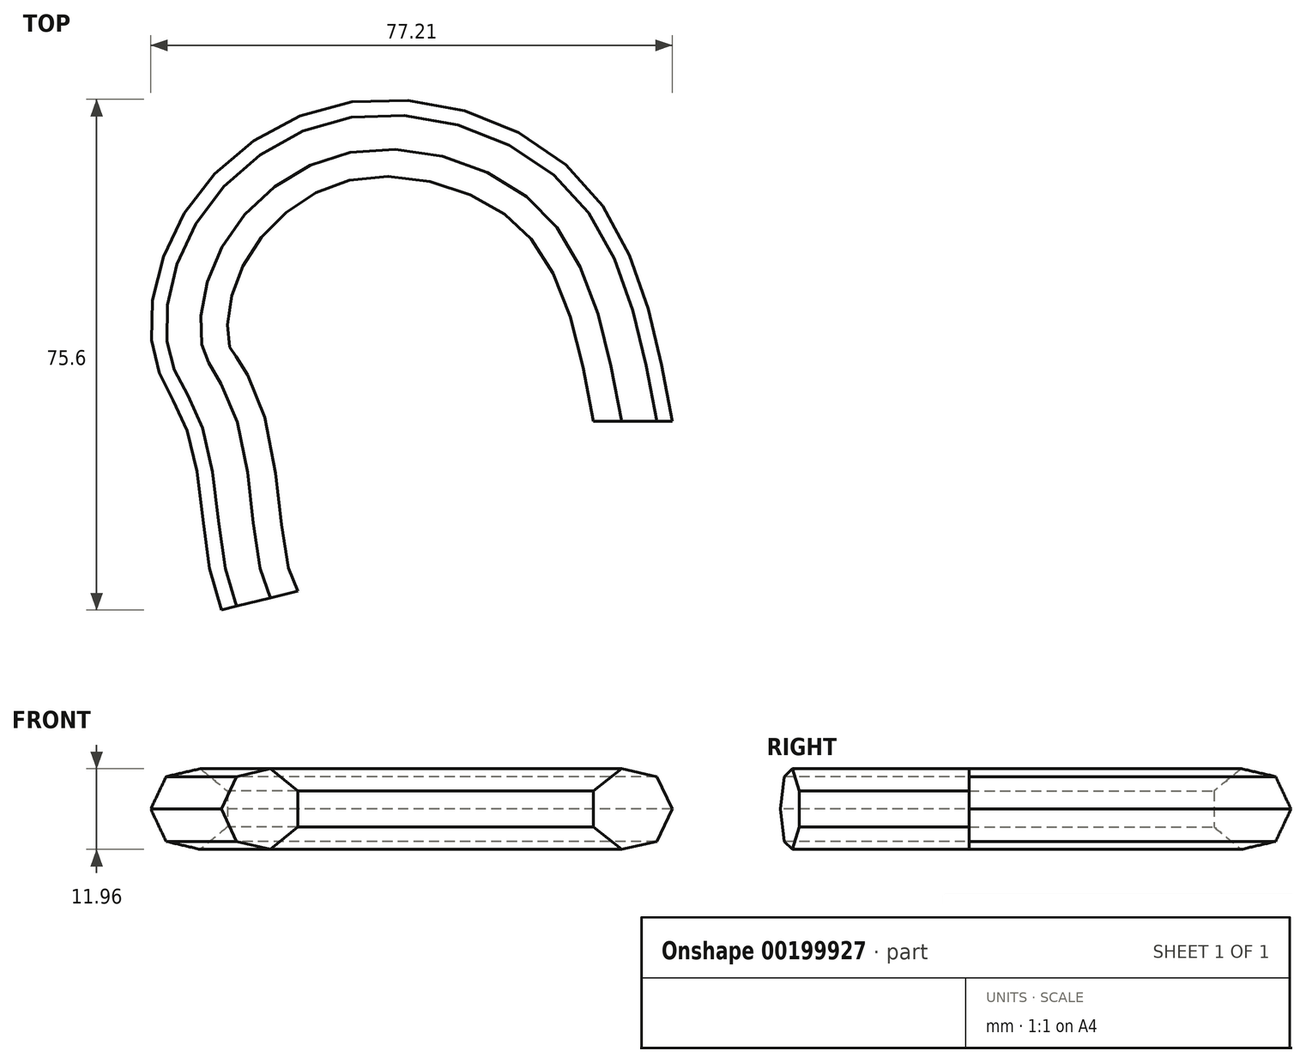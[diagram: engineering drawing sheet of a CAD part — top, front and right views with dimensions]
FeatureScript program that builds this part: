
annotation { "Feature Type Name" : "Feature", "Feature Type Description" : "" }
export const myFeature = defineFeature(function(context is Context, id is Id, definition is map)
    precondition{}
    {
        {
            var Q0;
            Q0=qCreatedBy(makeId("Top.planeOp"),FACE);
            var sketch = newSketch(context, id + "F0", { "sketchPlane" : qUnion([Q0])});
            skFitSpline(sketch, "E0", {"points": [v(56.92, 0) * mm, v(43.69, 35.53) * mm, v(8.92, 47.23) * mm, v(-16, 29.69) * mm, v(-19.7, 9.08) * mm, v(-14.46, -2.62) * mm, v(-9.83, -27.93) * mm], "startDerivative": vector(-33.46, 187.5) * mm, "endDerivative": vector(53.48, -120.24) * mm});
            skLineSegment(sketch, "E1", {"start": v(0, 0) * mm, "end": v(56.92, 0) * mm, "construction": true});
            skSolve(sketch);
        }
        {
            var Q0;
            Q0=qCreatedBy(makeId("Front.planeOp"),FACE);
            var sketch = newSketch(context, id + "F1", { "sketchPlane" : qUnion([Q0])});
            skCircle(sketch, "E2.cCircle", {"center": v(50.79, 0) * mm, "radius": 5.52 * mm, "construction": true});
            skLineSegment(sketch, "E2.0", {"start": v(56.92, 0) * mm, "end": v(54.6, -4.8) * mm});
            skLineSegment(sketch, "E2.1", {"start": v(54.6, -4.8) * mm, "end": v(49.42, -5.98) * mm});
            skLineSegment(sketch, "E2.2", {"start": v(49.42, -5.98) * mm, "end": v(45.26, -2.66) * mm});
            skLineSegment(sketch, "E2.3", {"start": v(45.26, -2.66) * mm, "end": v(45.26, 2.66) * mm});
            skLineSegment(sketch, "E2.4", {"start": v(45.26, 2.66) * mm, "end": v(49.42, 5.98) * mm});
            skLineSegment(sketch, "E2.5", {"start": v(49.42, 5.98) * mm, "end": v(54.6, 4.8) * mm});
            skLineSegment(sketch, "E2.6", {"start": v(54.6, 4.8) * mm, "end": v(56.92, 0) * mm});
            skPoint(sketch, "E2.0.midPoint", {"position": v(55.76, -2.4) * mm});
            skSolve(sketch);
        }
        {
            var Q0;
            Q0=makeQuery(id+"F1.imprint","IMPRINT",FACE,{"disambiguationData":[TD([[makeQuery(id+"F1.imprint","IMPRINT",EDGE,{"derivedFrom":sQuery(id+"F1.wireOp",EDGE,"E2.0")}),-1.0]])]});
            var Q1;
            Q1=sQuery(id+"F0.wireOp",EDGE,"E0");
            sweep(context, id + "F2", {"profiles" : qUnion([Q0]), "path" : qUnion([Q1])});
        }
    });
